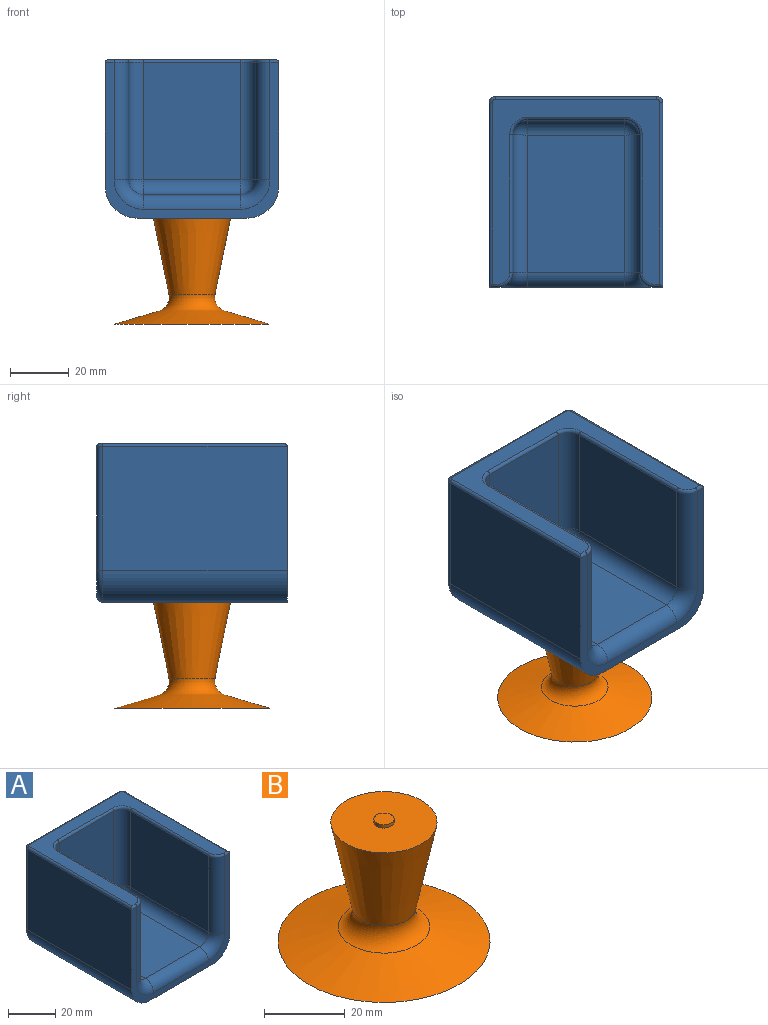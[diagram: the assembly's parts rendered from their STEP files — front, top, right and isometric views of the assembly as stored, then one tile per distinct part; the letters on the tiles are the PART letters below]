
ASSEMBLY  parts=2 mates=1
PART A: 45 faces, bbox 61.5x65.4x55.4 mm
  f0: plane 62.8x41.9mm, normal (1,0,0), area 2631.5mm2, adj f4,f23,f28,f40
  f1: plane 62.8x56.97mm, normal (0,0,1), area 1031.6mm2, adj f29,f30,f31,f32,f33,f34,f35,f36
  f2: plane 62.8x41.9mm, normal (-1,0,0), area 2631.5mm2, adj f4,f22,f24,f32
  f3: plane 62.8x37.24mm, normal (0,0,-1), area 2319.2mm2, adj f4,f22,f23,f26,f43
  f4: plane 58.97x52.77mm, normal (0,-1,0), area 467.8mm2, adj f0,f2,f3,f15,f17,f19,f20,f21
  f5: plane 54.97x50.77mm, normal (0,1,0), area 2756.9mm2, adj f24,f25,f26,f27,f28,f36
  f6: plane 46.8x39.77mm, normal (-1,0,0), area 1861.1mm2, adj f10,f14,f15,f39
  f7: plane 46.8x39.77mm, normal (1,0,0), area 1861.1mm2, adj f12,f18,f21,f31
  f8: plane 46.8x32.97mm, normal (0,0,1), area 1543mm2, adj f13,f14,f18,f19
  f9: plane 39.77x32.97mm, normal (0,-1,0), area 1311.1mm2, adj f10,f12,f13,f35
  f10: cylinder r=5mm len=39.77mm, axis (0,0,-1), area 312.3mm2, adj f6,f9,f11,f37
  f11: sphere r=5mm, area 39.3mm2, adj f10,f13,f14
  f12: cylinder r=5mm len=39.77mm, axis (0,0,1), area 312.3mm2, adj f7,f9,f16,f33
  f13: cylinder r=5mm len=32.97mm, axis (-1,0,0), area 258.9mm2, adj f8,f9,f11,f16
  f14: cylinder r=5mm len=46.8mm, axis (0,1,0), area 367.6mm2, adj f6,f8,f11,f17
  f15: cylinder r=5mm len=39.77mm, axis (0,0,1), area 312.3mm2, adj f4,f6,f17,f41
  f16: sphere r=5mm, area 39.3mm2, adj f12,f13,f18
  f17: torus R=10mm, axis (0,-1,0), area 84.1mm2, adj f4,f14,f15,f19
  f18: cylinder r=5mm len=46.8mm, axis (0,-1,0), area 367.6mm2, adj f7,f8,f16,f20
  f19: cylinder r=5mm len=32.97mm, axis (1,0,0), area 258.9mm2, adj f4,f8,f17,f20
  f20: torus R=10mm, axis (0,-1,0), area 84.1mm2, adj f4,f18,f19,f21
  f21: cylinder r=5mm len=39.77mm, axis (0,0,-1), area 312.3mm2, adj f4,f7,f20,f29
  f22: cylinder r=10.86mm len=62.8mm, axis (0,1,0), area 1071.7mm2, adj f2,f3,f4,f25
  f23: cylinder r=10.86mm len=62.8mm, axis (0,-1,0), area 1071.7mm2, adj f0,f3,f4,f27
  f24: cylinder r=2mm len=41.9mm, axis (0,0,-1), area 131.6mm2, adj f2,f5,f25,f34
  f25: torus R=8.86mm, axis (0,-1,0), area 50mm2, adj f5,f22,f24,f26
  f26: cylinder r=2mm len=37.24mm, axis (1,0,0), area 117mm2, adj f3,f5,f25,f27
  f27: torus R=8.86mm, axis (0,-1,0), area 50mm2, adj f5,f23,f26,f28
  f28: cylinder r=2mm len=41.9mm, axis (0,0,1), area 131.6mm2, adj f0,f5,f27,f38
  f29: torus R=4mm, axis (0,0,-1), area 11.4mm2, adj f1,f21,f30,f31
  f30: cylinder r=1mm len=3mm, axis (1,0,0), area 4.1mm2, adj f1,f4,f29,f32
  f31: cylinder r=1mm len=46.8mm, axis (0,1,0), area 73.5mm2, adj f1,f7,f29,f33
  f32: cylinder r=1mm len=62.8mm, axis (0,-1,0), area 98.1mm2, adj f1,f2,f30,f34
  f33: torus R=6mm, axis (0,0,-1), area 13.2mm2, adj f1,f12,f31,f35
  f34: torus R=1mm, axis (0,0,-1), area 4mm2, adj f1,f24,f32,f36
  f35: cylinder r=1mm len=32.97mm, axis (1,0,0), area 51.8mm2, adj f1,f9,f33,f37
  f36: cylinder r=1mm len=54.97mm, axis (-1,0,0), area 86.3mm2, adj f1,f5,f34,f38
  f37: torus R=6mm, axis (0,0,-1), area 13.2mm2, adj f1,f10,f35,f39
  f38: torus R=1mm, axis (0,0,-1), area 4mm2, adj f1,f28,f36,f40
  f39: cylinder r=1mm len=46.8mm, axis (0,-1,0), area 73.5mm2, adj f1,f6,f37,f41
  f40: cylinder r=1mm len=62.8mm, axis (0,1,0), area 98.1mm2, adj f0,f1,f38,f42
  f41: torus R=4mm, axis (0,0,-1), area 11.4mm2, adj f1,f15,f39,f42
  f42: cylinder r=1mm len=3mm, axis (1,0,0), area 4.1mm2, adj f1,f4,f40,f41
  f43: cylinder r=2.5mm len=5mm, axis (0,0,-1), area 15.7mm2, adj f3,f44
  f44: plane 5x5mm, normal (0,0,-1), area 19.6mm2, adj f43
PART B: 7 faces, bbox 52.4x52.4x37 mm
  f0: plane 52.4x52.4mm, normal (0,0,-1), area 2156.1mm2, adj f4
  f1: plane 26.24x26.24mm, normal (0,0,1), area 521.1mm2, adj f2,f5
  f2: cone r=13.12mm half-angle=11.6deg, axis (0,0,1), area 1734.2mm2, adj f1,f3
  f3: torus R=12.74mm, axis (0,0,-1), area 411.7mm2, adj f2,f4
  f4: cone r=11.32mm half-angle=73.4deg, axis (0,0,-1), area 1829.9mm2, adj f0,f3
  f5: cylinder r=2.5mm len=5mm, axis (0,0,-1), area 15.7mm2, adj f1,f6
  f6: plane 5x5mm, normal (0,0,1), area 19.6mm2, adj f5
PLACE A t=(-0.39,-0.22,0)mm fixed
PLACE B t=(-0.39,-0.22,-29.81)mm
MATE revolute B.f2 <-> A.f43  axis (0,0,1) through (-0.39,-0.22,-26.88)mm
